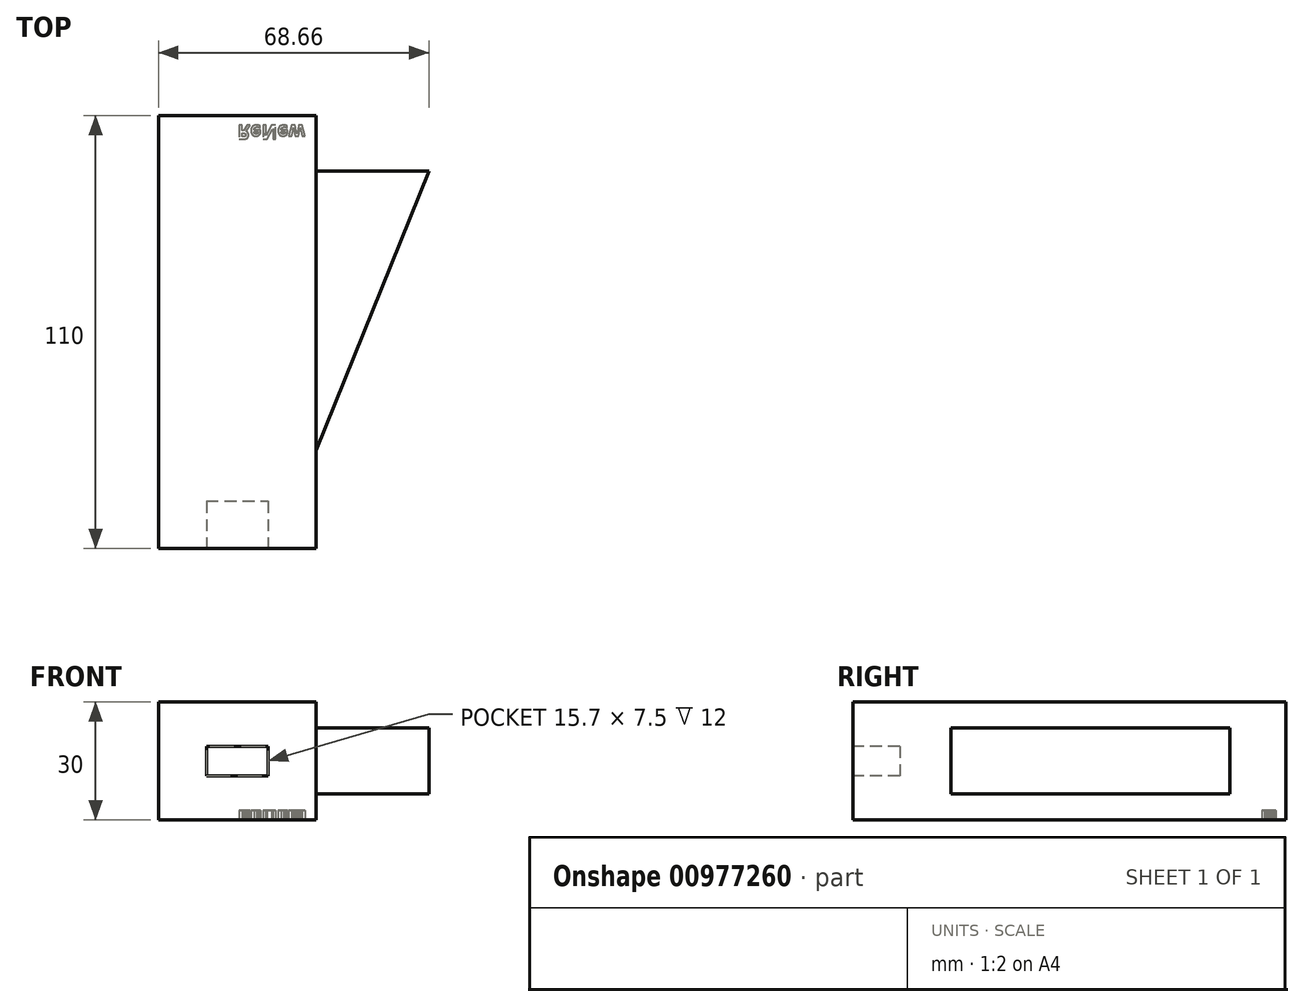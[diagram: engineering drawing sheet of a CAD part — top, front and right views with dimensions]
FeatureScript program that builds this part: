
annotation { "Feature Type Name" : "Feature", "Feature Type Description" : "" }
export const myFeature = defineFeature(function(context is Context, id is Id, definition is map)
    precondition{}
    {
        {
            var Q0;
            Q0=qCreatedBy(makeId("Top.planeOp"),FACE);
            var sketch = newSketch(context, id + "F0", { "sketchPlane" : qUnion([Q0])});
            skLineSegment(sketch, "E0.bottom", {"start": v(-20, 55) * mm, "end": v(20, 55) * mm});
            skLineSegment(sketch, "E0.top", {"start": v(-20, -55) * mm, "end": v(20, -55) * mm});
            skLineSegment(sketch, "E0.left", {"start": v(-20, 55) * mm, "end": v(-20, -55) * mm});
            skLineSegment(sketch, "E0.right", {"start": v(20, 55) * mm, "end": v(20, -55) * mm});
            skLineSegment(sketch, "E1", {"start": v(-20, -55) * mm, "end": v(20, 55) * mm, "construction": true});
            skPoint(sketch, "E2", {"position": v(0, 0) * mm});
            skSolve(sketch);
        }
        {
            var Q0;
            Q0=makeQuery(id+"F0.imprint","IMPRINT",FACE,{"disambiguationData":[TD([[makeQuery(id+"F0.imprint","IMPRINT",EDGE,{"derivedFrom":sQuery(id+"F0.wireOp",EDGE,"E0.bottom")}),-1.0]])]});
            extrude(context, id + "F1", {"entities" : qUnion([Q0]), "depth" : 30 * mm, "offsetDistance" : 25.4 * mm});
        }
        {
            var Q0;
            Q0=makeQuery(id+"F1.opExtrude","SWEPT_FACE",FACE,{"disambiguationData":[OSD([sQuery(id+"F0.wireOp",EDGE,"E0.right")])]});
            var sketch = newSketch(context, id + "F2", { "sketchPlane" : qUnion([Q0])});
            skLineSegment(sketch, "E3.bottom", {"start": v(40.84, 30) * mm, "end": v(-40.84, 30) * mm});
            skLineSegment(sketch, "E3.top", {"start": v(40.84, 0) * mm, "end": v(-40.84, 0) * mm});
            skLineSegment(sketch, "E3.left", {"start": v(40.84, 30) * mm, "end": v(40.84, 0) * mm});
            skLineSegment(sketch, "E3.right", {"start": v(-40.84, 30) * mm, "end": v(-40.84, 0) * mm});
            skLineSegment(sketch, "E4", {"start": v(40.84, 15) * mm, "end": v(55, 15) * mm, "construction": true});
            skLineSegment(sketch, "E5", {"start": v(-40.84, 15) * mm, "end": v(-55, 15) * mm, "construction": true});
            skLineSegment(sketch, "E6", {"start": v(40.84, 23.4) * mm, "end": v(-40.84, 23.4) * mm});
            skLineSegment(sketch, "E7", {"start": v(-40.84, 23.4) * mm, "end": v(40.84, 6.6) * mm, "construction": true});
            skLineSegment(sketch, "E8", {"start": v(40.84, 6.6) * mm, "end": v(-40.84, 6.6) * mm});
            skLineSegment(sketch, "E9", {"start": v(-20, 6.6) * mm, "end": v(-20, 0) * mm, "construction": true});
            skLineSegment(sketch, "E10", {"start": v(-20, 23.4) * mm, "end": v(-20, 30) * mm, "construction": true});
            skSolve(sketch);
        }
        {
            var Q0;
            {var subQ0=sQuery(id+"F2.wireOp",EDGE,"E6");Q0=makeQuery(id+"F2.imprint","IMPRINT",FACE,{"disambiguationData":[TD([[makeQuery(id+"F2.imprint","IMPRINT",EDGE,{"derivedFrom":subQ0}),1.0]])]});}
            extrude(context, id + "F3", {"entities" : qUnion([Q0]), "operationType" : NewBodyOperationType.ADD, "depth" : 30 * mm, "offsetDistance" : 25.4 * mm});
        }
        {
            var Q0;
            Q0=makeQuery(id+"F3.opExtrude","CAP_EDGE",EDGE,{"disambiguationData":[OSD([sQuery(id+"F2.wireOp",EDGE,"E3.right")])],"isStart":false});
            chamfer(context, id + "F4", {"entities" : qUnion([Q0]), "chamferType" : ChamferType.OFFSET_ANGLE, "width" : 85 * mm, "oppositeDirection" : false, "angle" : 22 * degree, "tangentPropagation" : true});
        }
        {
            var Q0;
            Q0=makeQuery(id+"F1.opExtrude","SWEPT_FACE",FACE,{"disambiguationData":[OSD([sQuery(id+"F0.wireOp",EDGE,"E0.top")])]});
            var sketch = newSketch(context, id + "F5", { "sketchPlane" : qUnion([Q0])});
            skLineSegment(sketch, "E11.bottom", {"start": v(-7.85, 18.75) * mm, "end": v(7.85, 18.75) * mm});
            skLineSegment(sketch, "E11.top", {"start": v(-7.85, 11.25) * mm, "end": v(7.85, 11.25) * mm});
            skLineSegment(sketch, "E11.left", {"start": v(-7.85, 18.75) * mm, "end": v(-7.85, 11.25) * mm});
            skLineSegment(sketch, "E11.right", {"start": v(7.85, 18.75) * mm, "end": v(7.85, 11.25) * mm});
            skLineSegment(sketch, "E12", {"start": v(-7.85, 15) * mm, "end": v(-20, 15) * mm, "construction": true});
            skLineSegment(sketch, "E13", {"start": v(7.85, 15) * mm, "end": v(20, 15) * mm, "construction": true});
            skLineSegment(sketch, "E14", {"start": v(-4.37, 18.75) * mm, "end": v(-4.37, 30) * mm, "construction": true});
            skLineSegment(sketch, "E15", {"start": v(-4.37, 30) * mm, "end": v(-4.37, 11.25) * mm, "construction": true});
            skLineSegment(sketch, "E16", {"start": v(-4.37, 11.25) * mm, "end": v(-4.37, 0) * mm, "construction": true});
            skLineSegment(sketch, "E17", {"start": v(-4.37, 0) * mm, "end": v(-5.12, -0.65) * mm, "construction": true});
            skSolve(sketch);
        }
        {
            var Q0;
            Q0=makeQuery(id+"F5.imprint","IMPRINT",FACE,{"disambiguationData":[TD([[makeQuery(id+"F5.imprint","IMPRINT",EDGE,{"derivedFrom":sQuery(id+"F5.wireOp",EDGE,"E11.bottom")}),-1.0]])]});
            extrude(context, id + "F6", {"entities" : qUnion([Q0]), "operationType" : NewBodyOperationType.REMOVE, "oppositeDirection" : true, "depth" : 12 * mm, "offsetDistance" : 25.4 * mm});
        }
        {
            var Q0;
            Q0=makeQuery(id+"F1.opExtrude","CAP_FACE",FACE,{"disambiguationData":[OSD([sQuery(id+"F0.wireOp",EDGE,"E0.bottom"),sQuery(id+"F0.wireOp",EDGE,"E0.top"),sQuery(id+"F0.wireOp",EDGE,"E0.left"),sQuery(id+"F0.wireOp",EDGE,"E0.right")])],"isStart":true});
            var sketch = newSketch(context, id + "F7", { "sketchPlane" : qUnion([Q0])});
            skText(sketch, "E18", { "text": "ReNew", "fontName": "OpenSans-Bold.ttf"});
            skLineSegment(sketch, "E19.bottom", {"start": v(17.5, -52.5) * mm, "end": v(20, -52.5) * mm, "construction": true});
            skLineSegment(sketch, "E19.top", {"start": v(17.5, -55) * mm, "end": v(20, -55) * mm, "construction": true});
            skLineSegment(sketch, "E19.left", {"start": v(17.5, -52.5) * mm, "end": v(17.5, -55) * mm, "construction": true});
            skLineSegment(sketch, "E19.right", {"start": v(20, -52.5) * mm, "end": v(20, -55) * mm, "construction": true});
            const initialGuessF7  = {"E18": [0, -0.0525, 1, 0, 0.00353]};
            skSetInitialGuess(sketch, initialGuessF7);
            skSolve(sketch);
        }
        {
            var Q0;
            Q0 = qSketchRegion(id + "F7", true);
            extrude(context, id + "F8", {"entities" : qUnion([Q0]), "operationType" : NewBodyOperationType.REMOVE, "oppositeDirection" : true, "depth" : 2.5 * mm, "offsetDistance" : 25.4 * mm});
        }
    });
